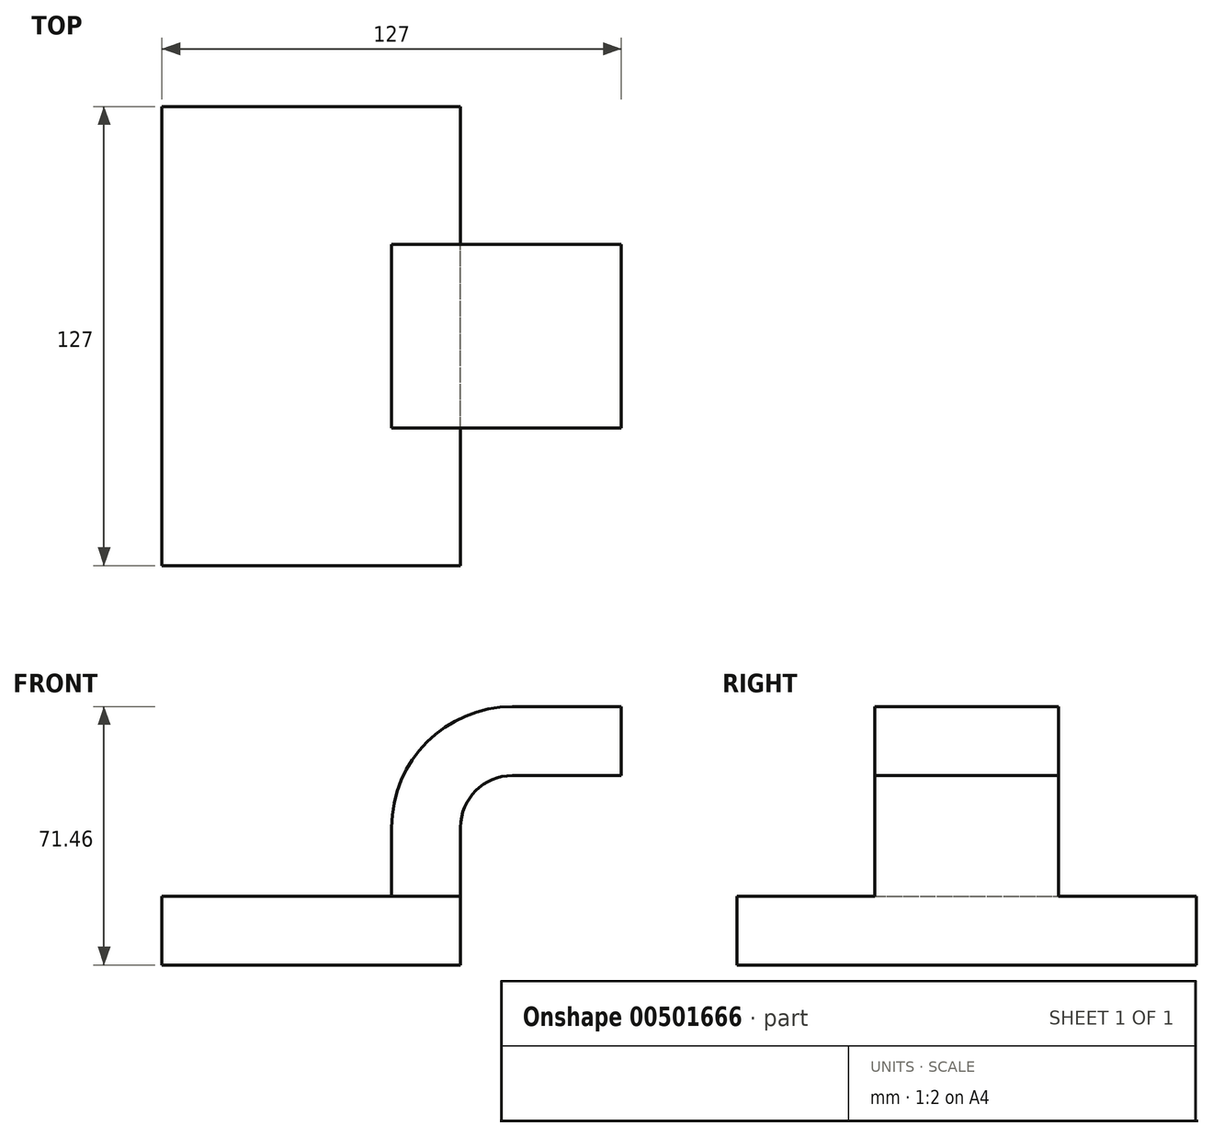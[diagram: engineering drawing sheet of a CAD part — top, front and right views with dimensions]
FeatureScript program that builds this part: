
annotation { "Feature Type Name" : "Feature", "Feature Type Description" : "" }
export const myFeature = defineFeature(function(context is Context, id is Id, definition is map)
    precondition{}
    {
        {
            var Q0;
            Q0=qCreatedBy(makeId("Front.planeOp"),FACE);
            var sketch = newSketch(context, id + "F0", { "sketchPlane" : qUnion([Q0])});
            skLineSegment(sketch, "E0.bottom", {"start": v(-41.28, 9.52) * mm, "end": v(41.27, 9.53) * mm});
            skLineSegment(sketch, "E0.top", {"start": v(-41.28, -9.53) * mm, "end": v(41.28, -9.53) * mm});
            skLineSegment(sketch, "E0.left", {"start": v(-41.28, 9.52) * mm, "end": v(-41.28, -9.53) * mm});
            skLineSegment(sketch, "E0.right", {"start": v(41.27, 9.53) * mm, "end": v(41.28, -9.52) * mm});
            skPoint(sketch, "E0.middle", {"position": v(0, 0) * mm});
            skLineSegment(sketch, "E1.bottom", {"start": v(60.53, 66.67) * mm, "end": v(111.33, 66.67) * mm});
            skLineSegment(sketch, "E1.top", {"start": v(60.53, 38.1) * mm, "end": v(111.33, 38.1) * mm});
            skLineSegment(sketch, "E1.left", {"start": v(60.53, 66.67) * mm, "end": v(60.53, 38.1) * mm});
            skLineSegment(sketch, "E1.right", {"start": v(111.33, 66.67) * mm, "end": v(111.33, 38.1) * mm});
            skPoint(sketch, "E1.middle", {"position": v(85.93, 52.39) * mm});
            skLineSegment(sketch, "E2", {"start": v(41.27, 9.53) * mm, "end": v(41.27, 28.55) * mm});
            skArc(sketch, "E3", {"start": v(41.27, 28.55) * mm, "mid": v(45.47, 38.68) * mm, "end": v(55.6, 42.88) * mm});
            skLineSegment(sketch, "E4", {"start": v(55.6, 42.88) * mm, "end": v(85.72, 42.88) * mm});
            skLineSegment(sketch, "E5.0", {"start": v(55.6, 61.93) * mm, "end": v(85.72, 61.93) * mm});
            skArc(sketch, "E5.1", {"start": v(22.22, 28.55) * mm, "mid": v(32, 52.15) * mm, "end": v(55.6, 61.93) * mm});
            skLineSegment(sketch, "E5.2", {"start": v(22.22, 9.53) * mm, "end": v(22.22, 28.55) * mm});
            skLineSegment(sketch, "E6", {"start": v(85.72, 61.93) * mm, "end": v(85.72, 42.88) * mm});
            skFitSpline(sketch, "E7", {"points": [v(-41.28, 9.52) * mm, v(55.6, 61.93) * mm], "startDerivative": vector(111.2, 0) * mm, "endDerivative": vector(214.46, -40.65) * mm});
            skSolve(sketch);
        }
        {
            var Q0;
            Q0=makeQuery(id+"F0.imprint","IMPRINT",FACE,{"disambiguationData":[TD([[makeQuery(id+"F0.imprint","IMPRINT",EDGE,{"derivedFrom":sQuery(id+"F0.wireOp",EDGE,"E0.top")}),1.0]])]});
            extrude(context, id + "F1", {"entities" : qUnion([Q0]), "endBound" : BoundingType.SYMMETRIC, "depth" : 127 * mm});
        }
        {
            var Q0;
            {var subQ1=sQuery(id+"F0.wireOp",EDGE,"E2");Q0=makeQuery(id+"F0.imprint","IMPRINT",FACE,{"disambiguationData":[TD([[makeQuery(id+"F0.imprint","IMPRINT",EDGE,{"derivedFrom":subQ1}),1.0]])]});}
            var Q1;
            {var subQ5=sQuery(id+"F0.wireOp",EDGE,"E6");Q1=makeQuery(id+"F0.imprint","IMPRINT",FACE,{"disambiguationData":[TD([[makeQuery(id+"F0.imprint","IMPRINT",EDGE,{"derivedFrom":subQ5}),-1.0]])]});}
            var Q2;
            Q2=makeQuery(id+"F0.imprint","IMPRINT",FACE,{"disambiguationData":[TD([[makeQuery(id+"F0.imprint","IMPRINT",EDGE,{"derivedFrom":sQuery(id+"F0.wireOp",EDGE,"E5.1")}),1.0]])]});
            extrude(context, id + "F2", {"entities" : qUnion([Q0, Q1, Q2]), "operationType" : NewBodyOperationType.ADD, "endBound" : BoundingType.SYMMETRIC, "depth" : 50.8 * mm});
        }
    });
